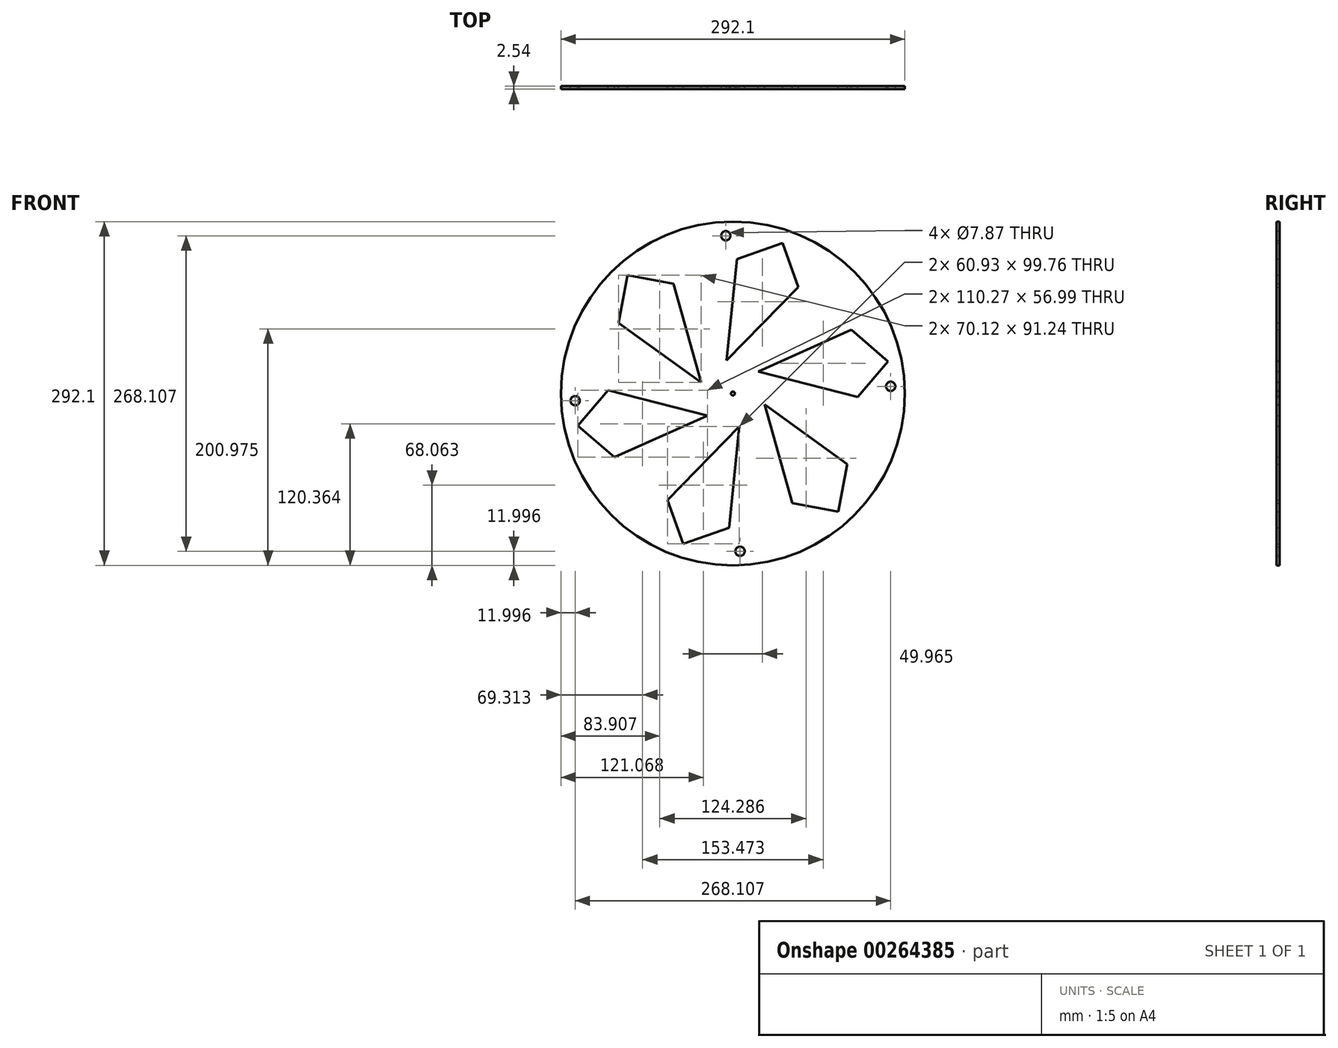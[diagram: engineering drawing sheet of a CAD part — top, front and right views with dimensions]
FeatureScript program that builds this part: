
annotation { "Feature Type Name" : "Feature", "Feature Type Description" : "" }
export const myFeature = defineFeature(function(context is Context, id is Id, definition is map)
    precondition{}
    {
        {
            var Q0;
            Q0=qCreatedBy(makeId("Front.planeOp"),FACE);
            var sketch = newSketch(context, id + "F0", { "sketchPlane" : qUnion([Q0])});
            skCircle(sketch, "E0", {"center": v(0, 0) * mm, "radius": 146.05 * mm});
            skCircle(sketch, "E1", {"center": v(0, 0) * mm, "radius": 1.65 * mm});
            skLineSegment(sketch, "E2", {"start": v(-1.65, 0) * mm, "end": v(1.65, 0) * mm});
            skLineSegment(sketch, "E3", {"start": v(-27.08, 9.3) * mm, "end": v(-97.2, 60) * mm});
            skLineSegment(sketch, "E4", {"start": v(-97.2, 60) * mm, "end": v(-89.6, 100.54) * mm});
            skLineSegment(sketch, "E5", {"start": v(-89.6, 100.54) * mm, "end": v(-50.58, 93.23) * mm});
            skLineSegment(sketch, "E6", {"start": v(-50.58, 93.23) * mm, "end": v(-27.08, 9.3) * mm});
            skLineSegment(sketch, "E7.1.1", {"start": v(-21.6, -18.8) * mm, "end": v(-100.56, -54.18) * mm});
            skLineSegment(sketch, "E7.1.2", {"start": v(-106.03, 2.81) * mm, "end": v(-21.6, -18.8) * mm});
            skLineSegment(sketch, "E7.1.3", {"start": v(-100.56, -54.18) * mm, "end": v(-131.87, -27.32) * mm});
            skLineSegment(sketch, "E7.1.4", {"start": v(-131.87, -27.32) * mm, "end": v(-106.03, 2.81) * mm});
            skLineSegment(sketch, "E7.2.1", {"start": v(5.48, -28.1) * mm, "end": v(-3.35, -114.18) * mm});
            skLineSegment(sketch, "E7.2.2", {"start": v(-55.45, -90.42) * mm, "end": v(5.48, -28.1) * mm});
            skLineSegment(sketch, "E7.2.3", {"start": v(-3.35, -114.18) * mm, "end": v(-42.27, -127.87) * mm});
            skLineSegment(sketch, "E7.2.4", {"start": v(-42.27, -127.87) * mm, "end": v(-55.45, -90.42) * mm});
            skLineSegment(sketch, "E7.3.1", {"start": v(27.08, -9.3) * mm, "end": v(97.2, -60) * mm});
            skLineSegment(sketch, "E7.3.2", {"start": v(50.58, -93.23) * mm, "end": v(27.08, -9.3) * mm});
            skLineSegment(sketch, "E7.3.3", {"start": v(97.2, -60) * mm, "end": v(89.6, -100.54) * mm});
            skLineSegment(sketch, "E7.3.4", {"start": v(89.6, -100.54) * mm, "end": v(50.58, -93.23) * mm});
            skLineSegment(sketch, "E7.4.1", {"start": v(21.6, 18.8) * mm, "end": v(100.56, 54.18) * mm});
            skLineSegment(sketch, "E7.4.2", {"start": v(106.03, -2.81) * mm, "end": v(21.6, 18.8) * mm});
            skLineSegment(sketch, "E7.4.3", {"start": v(100.56, 54.18) * mm, "end": v(131.87, 27.32) * mm});
            skLineSegment(sketch, "E7.4.4", {"start": v(131.87, 27.32) * mm, "end": v(106.03, -2.81) * mm});
            skLineSegment(sketch, "E7.5.1", {"start": v(-5.48, 28.1) * mm, "end": v(3.35, 114.18) * mm});
            skLineSegment(sketch, "E7.5.2", {"start": v(55.45, 90.42) * mm, "end": v(-5.48, 28.1) * mm});
            skLineSegment(sketch, "E7.5.3", {"start": v(3.35, 114.18) * mm, "end": v(42.27, 127.87) * mm});
            skLineSegment(sketch, "E7.5.4", {"start": v(42.27, 127.87) * mm, "end": v(55.45, 90.42) * mm});
            skCircle(sketch, "E8", {"center": v(-6.08, 134.05) * mm, "radius": 3.94 * mm});
            skCircle(sketch, "E9.1.0", {"center": v(-134.05, -6.08) * mm, "radius": 3.94 * mm});
            skCircle(sketch, "E9.2.0", {"center": v(6.08, -134.05) * mm, "radius": 3.94 * mm});
            skCircle(sketch, "E10.1.3.0", {"center": v(134.05, 6.08) * mm, "radius": 3.94 * mm});
            skSolve(sketch);
        }
        {
            var Q0;
            Q0 = qSketchRegion(id + "F0", true);
            extrude(context, id + "F1", {"entities" : qUnion([Q0]), "depth" : 2.54 * mm});
        }
    });
